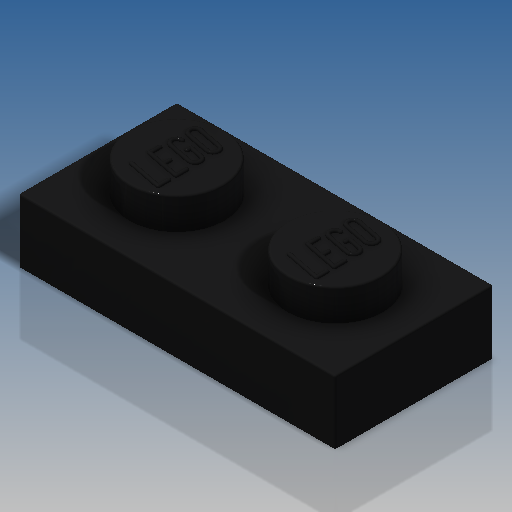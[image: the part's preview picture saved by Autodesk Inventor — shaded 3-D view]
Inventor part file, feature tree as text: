
AUTODESK INVENTOR PART (.ipt)
format: ipt  version: 2018.3 (Build 223284000, 284)  size: 1,480,192 bytes
history: native  units: in
note: dims shown in document units (in); Inventor stores cm internally (conversion verified against a paired STEP export)
features: extrude x4, sketch x4, fillet x2, pattern_linear x2, other x1
ambient origin geometry x8: Origin, YZ Plane, XZ Plane, XY Plane, X Axis, Y Axis, Z Axis, Center Point
bodies: Solid1 (feature_tree)
feature tree (13):
  extrude  "Extrusion1"  Depth=0.315in
  extrude  "Extrusion4"  Depth=0.063in
  other  "LEGO:1"
  fillet  "Fillet2"  Radius=0.063in
  pattern_linear  "Rectangular Pattern1"  Spacing1=0.189in  [1 undecoded]
  sketch  "Sketch3"  dims[d4=0.126in d5=0.0in d7=0.0591in d8=0.063in d11=0.063in d12=0.0in]
  extrude  "Extrusion2"  Depth=0.126in
  extrude  "Extrusion5"  Depth=0.126in
  pattern_linear  "Rectangular Pattern2"  Spacing1=0.063in  [1 undecoded]
  fillet  "Fillet1"  Radius=0.0039in
  sketch  "Sketch2"  dims[d0=0.6299in d1=0.315in]
  sketch  "Sketch9"  dims[d22=0.0039in]
  sketch  "Sketch10"  dims[d62=0.063in d63=0.189in d64=0.1575in d65=0.1575in d66=0.063in d67=0.0in d68=0.0039in d69=0.7874in d71=0.315in d72=0.3937in d74=0.315in d77=0.0709in d78=0.0in d79=0.3937in d81=0.315in d82=0.3937in d84=0.315in d85=0.126in d86=0.0in d87=0.0in d88=0.0in d89=0.0in d90=0.0in d91=0.0079in d92=0.0732in d93=0.0281in d94=0.035in d95=0.0079in d96=0.0139in d97=0.0281in d98=0.035in d99=0.0281in d100=0.0159in d101=0.0177in d102=0.035in d103=0.5428in]
note: 2 required parameter values undecoded (feature->parameter linkage not recoverable at this tier; creation-order binding heuristic only, values carry confidence <= 0.55)
